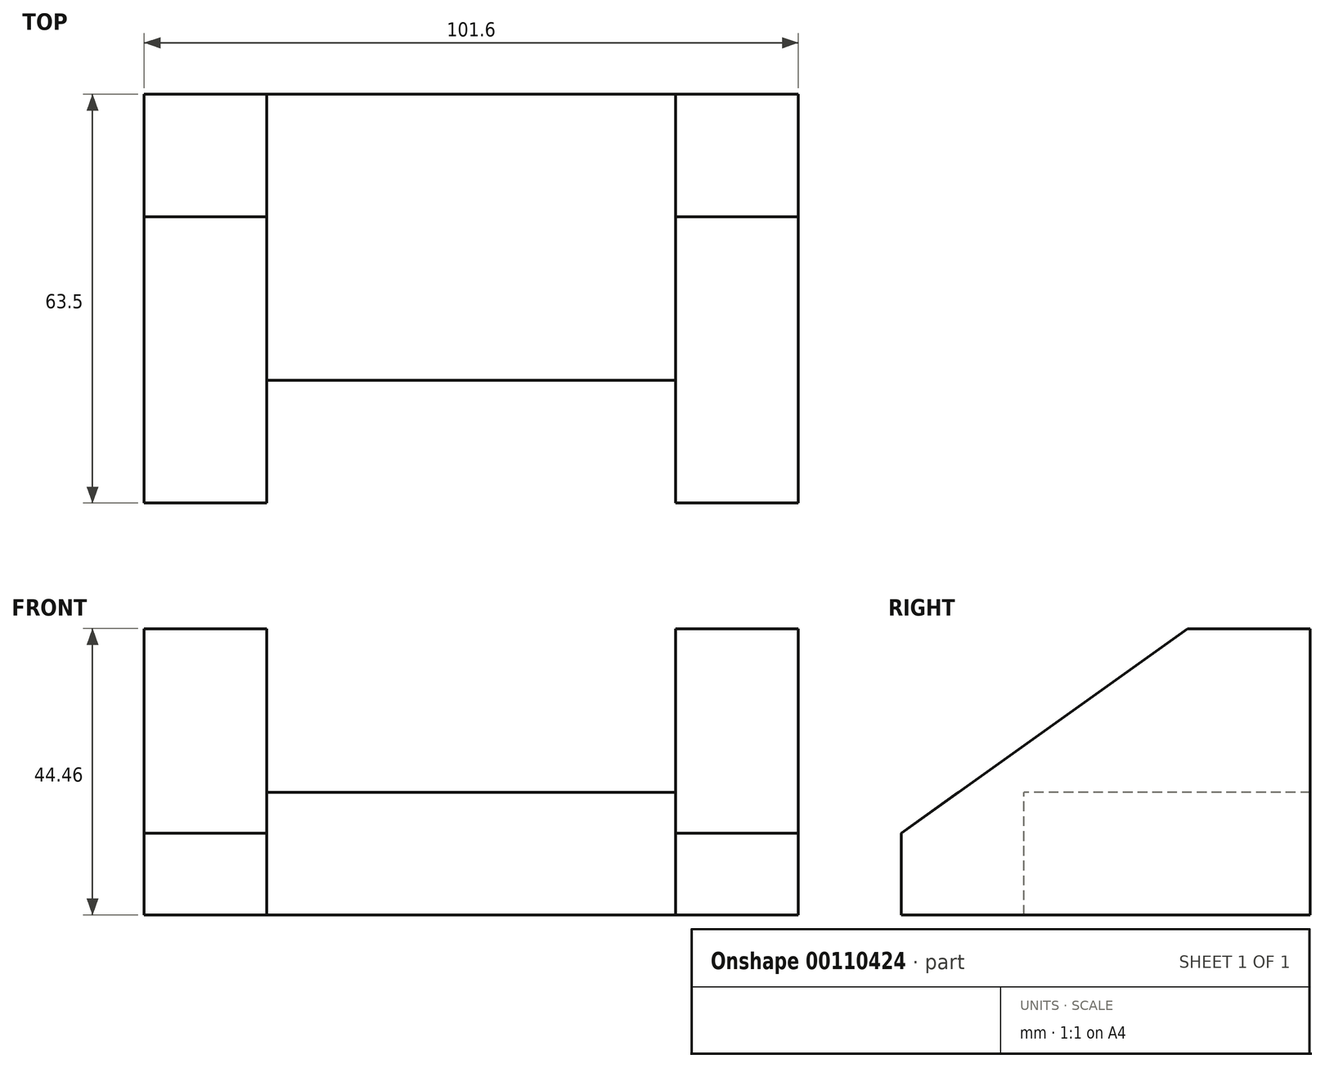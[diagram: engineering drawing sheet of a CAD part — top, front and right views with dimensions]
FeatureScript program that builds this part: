
annotation { "Feature Type Name" : "Feature", "Feature Type Description" : "" }
export const myFeature = defineFeature(function(context is Context, id is Id, definition is map)
    precondition{}
    {
        {
            var Q0;
            Q0=qCreatedBy(makeId("Top.planeOp"),FACE);
            var sketch = newSketch(context, id + "F0", { "sketchPlane" : qUnion([Q0])});
            skLineSegment(sketch, "E0.bottom", {"start": v(-36.65, 23.03) * mm, "end": v(26.85, 23.03) * mm});
            skLineSegment(sketch, "E0.top", {"start": v(-36.65, -21.42) * mm, "end": v(26.85, -21.42) * mm});
            skLineSegment(sketch, "E0.left", {"start": v(-36.65, 23.03) * mm, "end": v(-36.65, -21.42) * mm});
            skLineSegment(sketch, "E0.right", {"start": v(26.85, 23.03) * mm, "end": v(26.85, -21.42) * mm});
            skSolve(sketch);
        }
        {
            var Q0;
            Q0=makeQuery(id+"F0.imprint","IMPRINT",FACE,{"disambiguationData":[TD([[makeQuery(id+"F0.imprint","IMPRINT",EDGE,{"derivedFrom":sQuery(id+"F0.wireOp",EDGE,"E0.bottom")}),-1.0]])]});
            extrude(context, id + "F1", {"entities" : qUnion([Q0]), "oppositeDirection" : true, "depth" : 19.05 * mm});
        }
        {
            var Q0;
            Q0=makeQuery(id+"F1.opExtrude","SWEPT_FACE",FACE,{"disambiguationData":[OSD([sQuery(id+"F0.wireOp",EDGE,"E0.right")])]});
            var sketch = newSketch(context, id + "F2", { "sketchPlane" : qUnion([Q0])});
            skLineSegment(sketch, "E1", {"start": v(23.03, -19.05) * mm, "end": v(-40.47, -19.05) * mm});
            skLineSegment(sketch, "E2", {"start": v(-40.47, -19.05) * mm, "end": v(-40.47, -6.36) * mm});
            skLineSegment(sketch, "E3", {"start": v(23.03, -19.05) * mm, "end": v(23.03, 25.4) * mm});
            skLineSegment(sketch, "E4", {"start": v(23.03, 25.4) * mm, "end": v(3.98, 25.4) * mm});
            skLineSegment(sketch, "E5", {"start": v(3.98, 25.4) * mm, "end": v(-40.47, -6.36) * mm});
            skSolve(sketch);
        }
        {
            var Q0;
            {var subQ4=sQuery(id+"F2.wireOp",EDGE,"E2");Q0=makeQuery(id+"F2.imprint","IMPRINT",FACE,{"disambiguationData":[TD([[makeQuery(id+"F2.imprint","IMPRINT",EDGE,{"derivedFrom":subQ4}),-1.0]])]});}
            var Q1;
            {var subQ3=sQuery(id+"F0.wireOp",EDGE,"E0.right");var subQ5=makeQuery(id+"F1.opExtrude","CAP_EDGE",EDGE,{"disambiguationData":[OSD([subQ3])],"isStart":true});Q1=makeQuery(id+"F2.imprint","IMPRINT",FACE,{"disambiguationData":[TD([[makeQuery(id+"F2.imprint","IMPRINT",EDGE,{"derivedFrom":subQ5}),1.0]])]});}
            extrude(context, id + "F3", {"entities" : qUnion([Q0, Q1]), "operationType" : NewBodyOperationType.ADD, "depth" : 19.05 * mm});
        }
        {
            var Q0;
            Q0=makeQuery(id+"F1.opExtrude","SWEPT_FACE",FACE,{"disambiguationData":[OSD([sQuery(id+"F0.wireOp",EDGE,"E0.left")])]});
            var sketch = newSketch(context, id + "F4", { "sketchPlane" : qUnion([Q0])});
            skLineSegment(sketch, "E6", {"start": v(-23.03, -19.05) * mm, "end": v(-23.03, 25.4) * mm});
            skLineSegment(sketch, "E7", {"start": v(-23.03, 25.4) * mm, "end": v(-3.98, 25.4) * mm});
            skLineSegment(sketch, "E8", {"start": v(-3.98, 25.4) * mm, "end": v(40.47, -6.35) * mm});
            skLineSegment(sketch, "E9", {"start": v(40.47, -6.35) * mm, "end": v(40.47, -19.05) * mm});
            skLineSegment(sketch, "E10", {"start": v(40.47, -19.05) * mm, "end": v(-23.03, -19.05) * mm});
            skSolve(sketch);
        }
        {
            var Q0;
            {var subQ0=sQuery(id+"F4.wireOp",EDGE,"E7");Q0=makeQuery(id+"F4.imprint","IMPRINT",FACE,{"disambiguationData":[TD([[makeQuery(id+"F4.imprint","IMPRINT",EDGE,{"derivedFrom":subQ0}),-1.0]])]});}
            var Q1;
            {var subQ1=sQuery(id+"F0.wireOp",EDGE,"E0.left");var subQ2=makeQuery(id+"F1.opExtrude","CAP_EDGE",EDGE,{"disambiguationData":[OSD([subQ1])],"isStart":true});Q1=makeQuery(id+"F4.imprint","IMPRINT",FACE,{"disambiguationData":[TD([[makeQuery(id+"F4.imprint","IMPRINT",EDGE,{"derivedFrom":subQ2}),-1.0]])]});}
            extrude(context, id + "F5", {"entities" : qUnion([Q0, Q1]), "operationType" : NewBodyOperationType.ADD, "depth" : 19.05 * mm});
        }
    });
